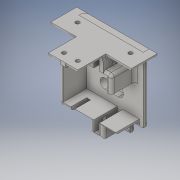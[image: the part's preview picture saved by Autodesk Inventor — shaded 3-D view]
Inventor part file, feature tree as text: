
AUTODESK INVENTOR PART (.ipt)
format: ipt  version: 2016 (Build 200138000, 138)  size: 415,232 bytes
history: native  units: in
note: dims shown in document units (in); Inventor stores cm internally (conversion verified against a paired STEP export)
features: sketch x15, other x3
ambient origin geometry x8: Origin, YZ Plane, XZ Plane, XY Plane, X Axis, Y Axis, Z Axis, Center Point
bodies: Solid1 (feature_tree)
feature tree (18):
  other  "Knee_holder_v3.ipt"
  other  "Solid1::Knee_holder_v3.ipt"
  other  "TaggingFeature1"
  sketch  "Sketch1"  dims[d0=0.3937in]
  sketch  "Sketch12"
  sketch  "Sketch22"
  sketch  "Sketch32"
  sketch  "Sketch35"
  sketch  "Sketch36"
  sketch  "Sketch41"
  sketch  "Sketch43"
  sketch  "Sketch46"
  sketch  "Sketch47"
  sketch  "Sketch48"
  sketch  "Sketch49"
  sketch  "Sketch50"
  sketch  "Sketch51"
  sketch  "Sketch52"
